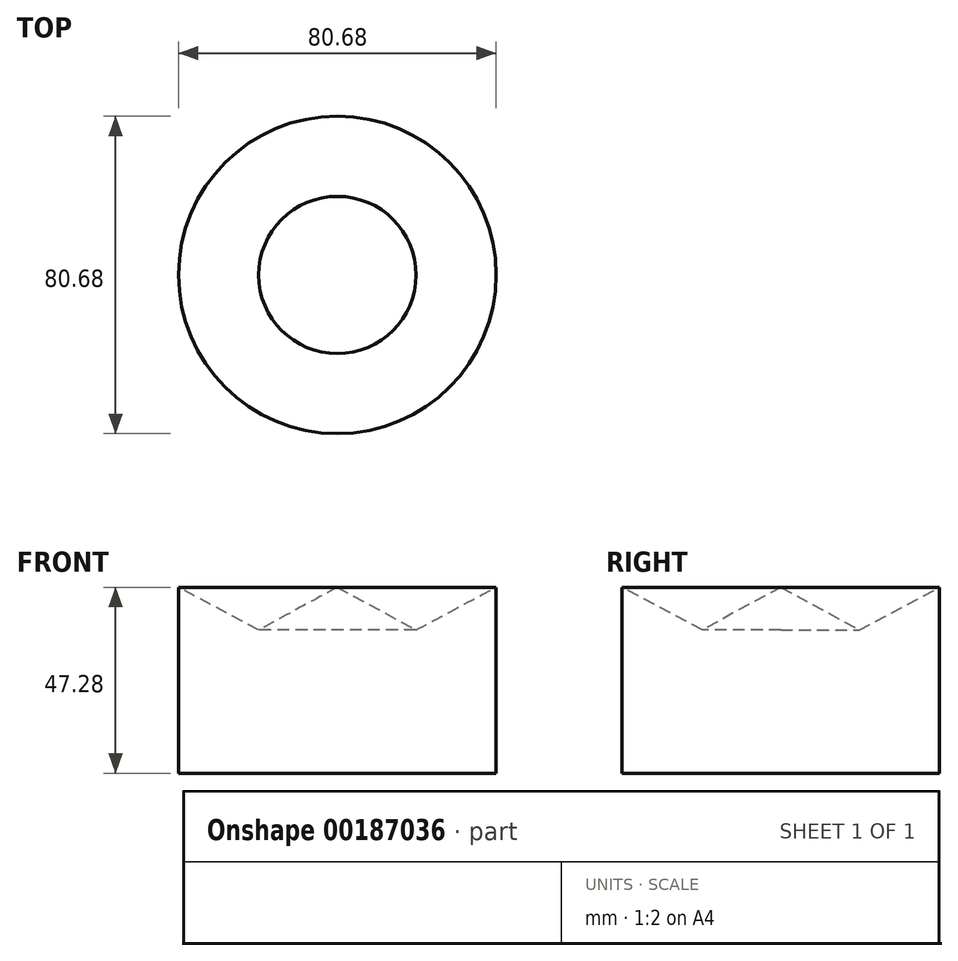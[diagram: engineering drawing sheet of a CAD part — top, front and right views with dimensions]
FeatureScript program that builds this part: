
annotation { "Feature Type Name" : "Feature", "Feature Type Description" : "" }
export const myFeature = defineFeature(function(context is Context, id is Id, definition is map)
    precondition{}
    {
        {
            var Q0;
            Q0=qCreatedBy(makeId("Front.planeOp"),FACE);
            var sketch = newSketch(context, id + "F0", { "sketchPlane" : qUnion([Q0])});
            skLineSegment(sketch, "E0", {"start": v(40.34, 0) * mm, "end": v(40.34, 47.28) * mm});
            skLineSegment(sketch, "E1", {"start": v(40.34, 47.28) * mm, "end": v(19.98, 36.44) * mm});
            skLineSegment(sketch, "E2", {"start": v(19.98, 36.44) * mm, "end": v(0, 47.28) * mm});
            skLineSegment(sketch, "E3", {"start": v(0, 47.28) * mm, "end": v(0, 0) * mm});
            skLineSegment(sketch, "E4", {"start": v(0, 0) * mm, "end": v(40.34, 0) * mm});
            skSolve(sketch);
        }
        {
            var Q0;
            Q0=makeQuery(id+"F0.imprint","IMPRINT",FACE,{"disambiguationData":[TD([[makeQuery(id+"F0.imprint","IMPRINT",EDGE,{"derivedFrom":sQuery(id+"F0.wireOp",EDGE,"E0")}),1.0]])]});
            var Q1;
            Q1=sQuery(id+"F0.wireOp",EDGE,"E3");
            revolve(context, id + "F1", {"entities" : qUnion([Q0]), "axis" : qUnion([Q1]), "revolveType" : RevolveType.FULL});
        }
    });
